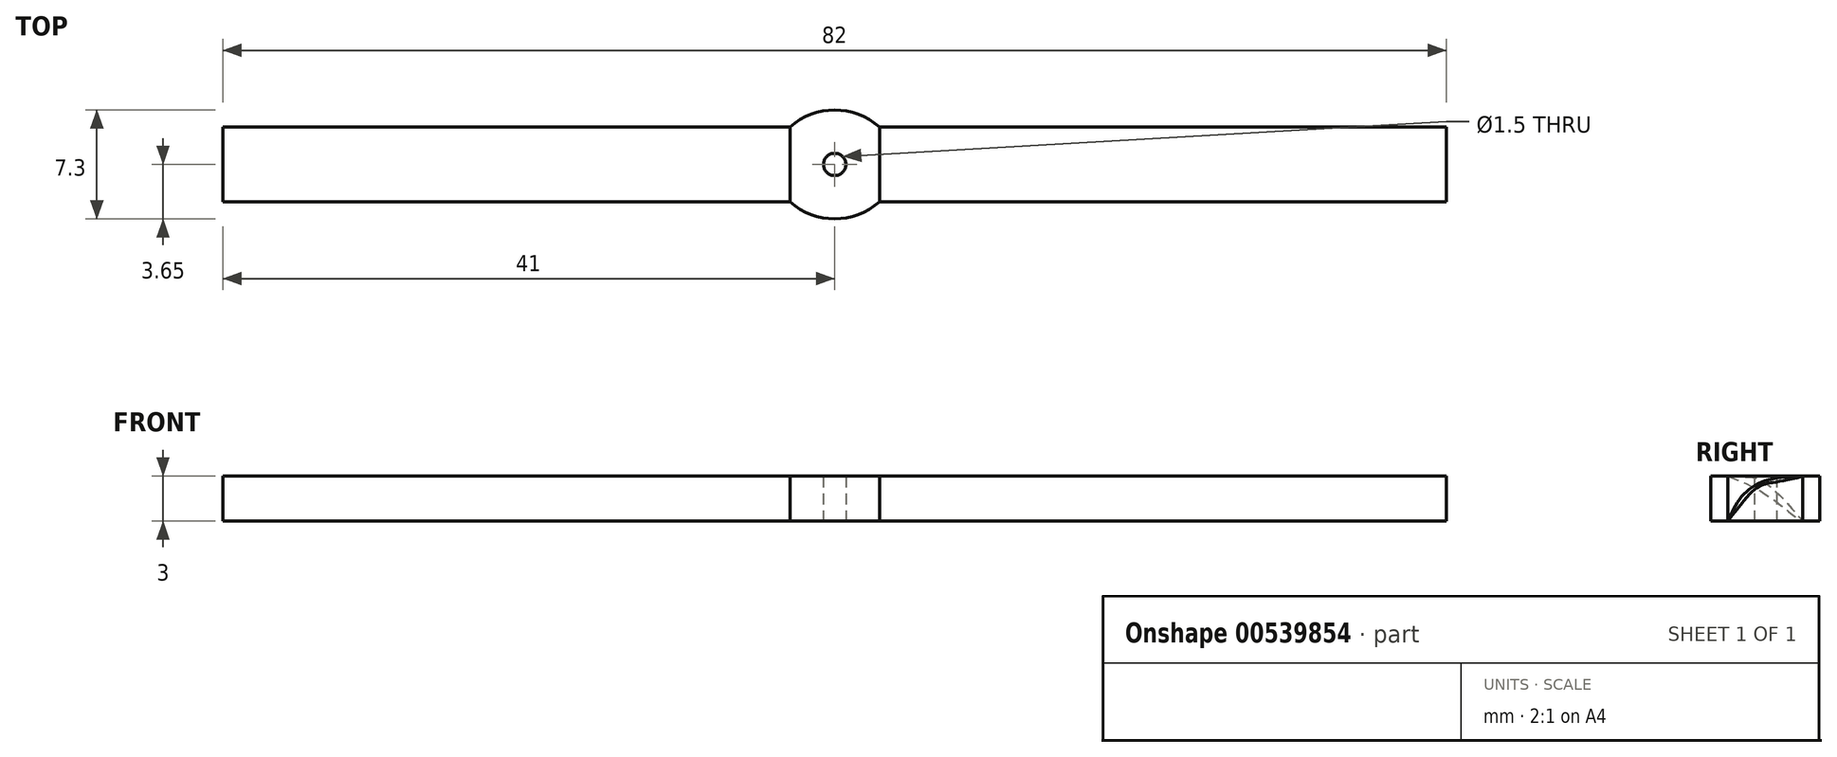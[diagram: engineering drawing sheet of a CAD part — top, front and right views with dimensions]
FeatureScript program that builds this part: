
annotation { "Feature Type Name" : "Feature", "Feature Type Description" : "" }
export const myFeature = defineFeature(function(context is Context, id is Id, definition is map)
    precondition{}
    {
        {
            var Q0;
            Q0=qCreatedBy(makeId("Top.planeOp"),FACE);
            var sketch = newSketch(context, id + "F0", { "sketchPlane" : qUnion([Q0])});
            skCircle(sketch, "E0", {"center": v(0, 0) * mm, "radius": 0.75 * mm});
            skLineSegment(sketch, "E1.bottom", {"start": v(3, -2.5) * mm, "end": v(41, -2.5) * mm});
            skLineSegment(sketch, "E1.top", {"start": v(3, 2.5) * mm, "end": v(41, 2.5) * mm});
            skLineSegment(sketch, "E1.right", {"start": v(41, -2.5) * mm, "end": v(41, 2.5) * mm});
            skLineSegment(sketch, "E2.bottom", {"start": v(-3, 2.5) * mm, "end": v(-41, 2.5) * mm});
            skLineSegment(sketch, "E2.top", {"start": v(-3, -2.5) * mm, "end": v(-41, -2.5) * mm});
            skLineSegment(sketch, "E2.right", {"start": v(-41, 2.5) * mm, "end": v(-41, -2.5) * mm});
            skLineSegment(sketch, "E3", {"start": v(0, 0) * mm, "end": v(0, 1.44) * mm, "construction": true});
            skLineSegment(sketch, "E4", {"start": v(0, 0) * mm, "end": v(1.35, 0) * mm, "construction": true});
            skArc(sketch, "E5", {"start": v(3, 2.5) * mm, "mid": v(0, 3.65) * mm, "end": v(-3, 2.5) * mm});
            skArc(sketch, "E6", {"start": v(-3, -2.5) * mm, "mid": v(0, -3.65) * mm, "end": v(3, -2.5) * mm});
            skSolve(sketch);
        }
        {
            var Q0;
            Q0=makeQuery(id+"F0.imprint","IMPRINT",FACE,{"disambiguationData":[TD([[makeQuery(id+"F0.imprint","IMPRINT",EDGE,{"derivedFrom":sQuery(id+"F0.wireOp",EDGE,"E0")}),-1.0]])]});
            extrude(context, id + "F1", {"entities" : qUnion([Q0]), "depth" : 3 * mm});
        }
        {
            var Q0;
            Q0=makeQuery(id+"F1.opExtrude","SWEPT_FACE",FACE,{"disambiguationData":[OSD([sQuery(id+"F0.wireOp",EDGE,"E2.right")])]});
            var sketch = newSketch(context, id + "F2", { "sketchPlane" : qUnion([Q0])});
            skLineSegment(sketch, "E7.0.0", {"start": v(-2.5, 0) * mm, "end": v(2.5, 0) * mm});
            skLineSegment(sketch, "E7.0.1", {"start": v(2.5, 0) * mm, "end": v(2.5, 3) * mm});
            skLineSegment(sketch, "E7.0.2", {"start": v(2.5, 3) * mm, "end": v(-2.5, 3) * mm});
            skLineSegment(sketch, "E7.0.3", {"start": v(-2.5, 3) * mm, "end": v(-2.5, 0) * mm});
            skFitSpline(sketch, "E8", {"points": [v(2.5, 3) * mm, v(-2.5, 0) * mm], "startDerivative": vector(-6.44, -0.49) * mm, "endDerivative": vector(-9, -10.44) * mm});
            skFitSpline(sketch, "E9", {"points": [v(2.5, 3) * mm, v(-2.5, 0) * mm], "startDerivative": vector(-10.34, -3.78) * mm, "endDerivative": vector(-2.42, -0.55) * mm});
            skSolve(sketch);
        }
        {
            var Q0;
            Q0=makeQuery(id+"F2.imprint","IMPRINT",FACE,{"disambiguationData":[TD([[makeQuery(id+"F2.imprint","IMPRINT",EDGE,{"derivedFrom":sQuery(id+"F2.wireOp",EDGE,"E7.0.2")}),-1.0]])]});
            var Q1;
            Q1=makeQuery(id+"F2.imprint","IMPRINT",FACE,{"disambiguationData":[TD([[makeQuery(id+"F2.imprint","IMPRINT",EDGE,{"derivedFrom":sQuery(id+"F2.wireOp",EDGE,"E7.0.0")}),1.0]])]});
            extrude(context, id + "F3", {"entities" : qUnion([Q0, Q1]), "operationType" : NewBodyOperationType.REMOVE, "oppositeDirection" : true, "depth" : 38 * mm});
        }
        {
            var Q0;
            Q0=makeQuery(id+"F1.opExtrude","SWEPT_FACE",FACE,{"disambiguationData":[OSD([sQuery(id+"F0.wireOp",EDGE,"E1.right")])]});
            var sketch = newSketch(context, id + "F4", { "sketchPlane" : qUnion([Q0])});
            skLineSegment(sketch, "E10.0.0", {"start": v(-2.5, 0) * mm, "end": v(2.5, 0) * mm});
            skLineSegment(sketch, "E10.0.1", {"start": v(2.5, 0) * mm, "end": v(2.5, 3) * mm});
            skLineSegment(sketch, "E10.0.2", {"start": v(2.5, 3) * mm, "end": v(-2.5, 3) * mm});
            skLineSegment(sketch, "E10.0.3", {"start": v(-2.5, 3) * mm, "end": v(-2.5, 0) * mm});
            skFitSpline(sketch, "E11", {"points": [v(2.5, 3) * mm, v(-2.5, 0) * mm], "startDerivative": vector(-9.08, 0) * mm, "endDerivative": vector(-2.72, -6.55) * mm});
            skFitSpline(sketch, "E12", {"points": [v(2.5, 3) * mm, v(-2.5, 0) * mm], "startDerivative": vector(-9.23, -2.7) * mm, "endDerivative": vector(-7.5, -9.98) * mm});
            skSolve(sketch);
        }
        {
            var Q0;
            Q0=makeQuery(id+"F4.imprint","IMPRINT",FACE,{"disambiguationData":[TD([[makeQuery(id+"F4.imprint","IMPRINT",EDGE,{"derivedFrom":sQuery(id+"F4.wireOp",EDGE,"E10.0.2")}),-1.0]])]});
            var Q1;
            Q1=makeQuery(id+"F4.imprint","IMPRINT",FACE,{"disambiguationData":[TD([[makeQuery(id+"F4.imprint","IMPRINT",EDGE,{"derivedFrom":sQuery(id+"F4.wireOp",EDGE,"E10.0.0")}),1.0]])]});
            extrude(context, id + "F5", {"entities" : qUnion([Q0, Q1]), "operationType" : NewBodyOperationType.REMOVE, "oppositeDirection" : true, "depth" : 38 * mm});
        }
    });
